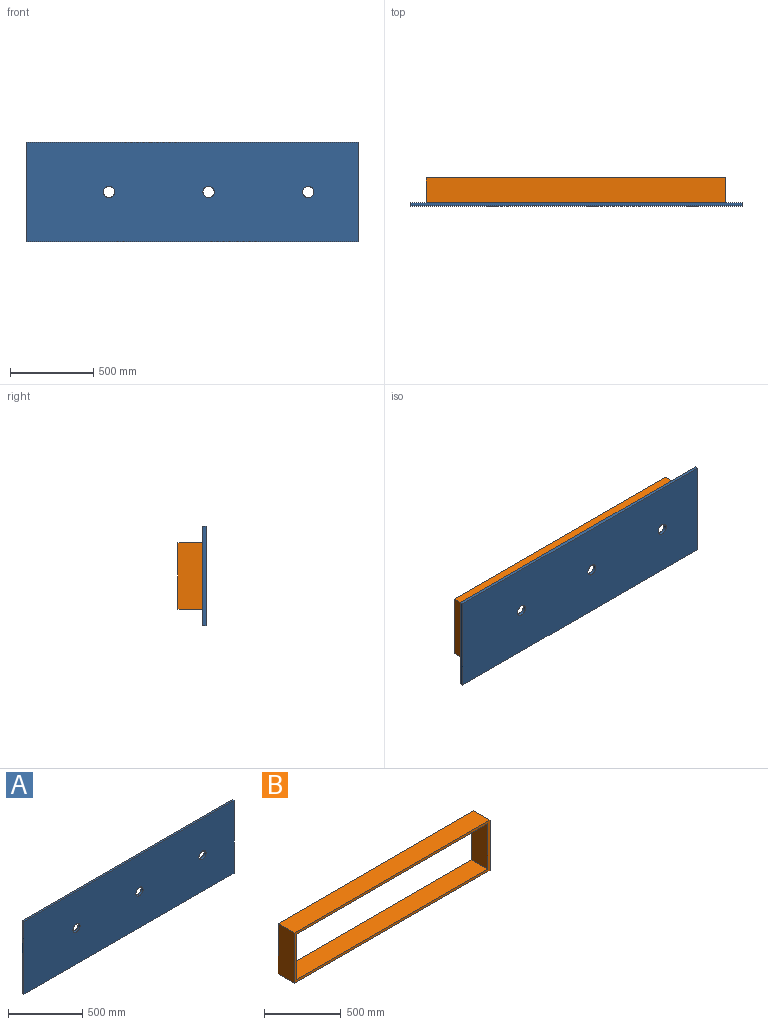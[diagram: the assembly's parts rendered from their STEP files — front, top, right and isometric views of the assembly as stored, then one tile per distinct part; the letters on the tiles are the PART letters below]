
ASSEMBLY  parts=2 mates=1
PART A: 9 faces, bbox 2000x19x600 mm
  f0: cylinder r=34mm len=68mm, axis (0,1,0), area 4058.9mm2, adj f5,f6
  f1: plane 600x19mm, normal (1,0,0), area 11400mm2, adj f2,f4,f5,f6
  f2: plane 2000x19mm, normal (0,0,-1), area 38000mm2, adj f1,f3,f5,f6
  f3: plane 600x19mm, normal (-1,0,0), area 11400mm2, adj f2,f4,f5,f6
  f4: plane 2000x19mm, normal (0,0,1), area 38000mm2, adj f1,f3,f5,f6
  f5: plane 2000x600mm, normal (0,1,0), area 1189105mm2, adj f0,f1,f2,f3,f4,f7,f8
  f6: plane 2000x600mm, normal (0,-1,0), area 1189105mm2, adj f0,f1,f2,f3,f4,f7,f8
  f7: cylinder r=34mm len=68mm, axis (0,1,0), area 4058.9mm2, adj f5,f6
  f8: cylinder r=34mm len=68mm, axis (0,1,0), area 4058.9mm2, adj f5,f6
PART B: 10 faces, bbox 1800x150x400 mm
  f0: plane 1800x400mm, normal (0,1,0), area 82156mm2, adj f2,f3,f4,f5,f6,f7,f8,f9
  f1: plane 1800x400mm, normal (0,-1,0), area 82156mm2, adj f2,f3,f4,f5,f6,f7,f8,f9
  f2: plane 400x150mm, normal (1,0,0), area 60000mm2, adj f0,f1,f3,f5
  f3: plane 1800x150mm, normal (0,0,-1), area 270000mm2, adj f0,f1,f2,f4
  f4: plane 400x150mm, normal (-1,0,0), area 60000mm2, adj f0,f1,f3,f5
  f5: plane 1800x150mm, normal (0,0,1), area 270000mm2, adj f0,f1,f2,f4
  f6: plane 362x150mm, normal (-1,0,0), area 54300mm2, adj f0,f1,f7,f9
  f7: plane 1762x150mm, normal (0,0,1), area 264300mm2, adj f0,f1,f6,f8
  f8: plane 362x150mm, normal (1,0,0), area 54300mm2, adj f0,f1,f7,f9
  f9: plane 1762x150mm, normal (0,0,-1), area 264300mm2, adj f0,f1,f6,f8
PLACE A t=(0.92,-19,0)mm
PLACE B at identity fixed
MATE planar B.f1 <-> A.f5  axis (0,-1,0) through (0,0,0)mm
